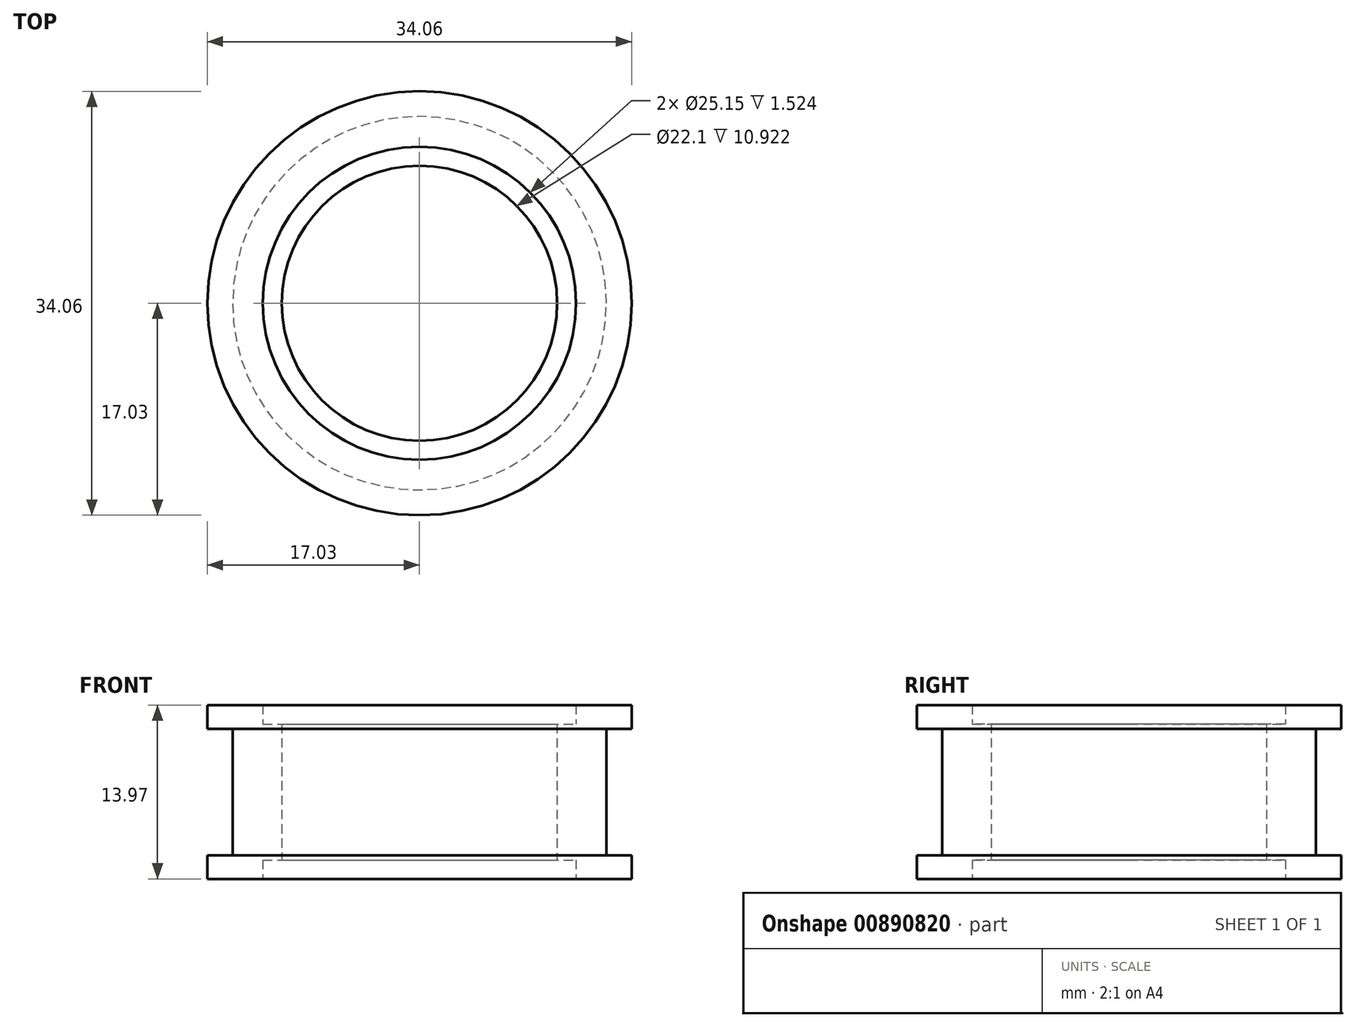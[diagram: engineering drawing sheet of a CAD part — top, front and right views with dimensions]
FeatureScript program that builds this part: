
annotation { "Feature Type Name" : "Feature", "Feature Type Description" : "" }
export const myFeature = defineFeature(function(context is Context, id is Id, definition is map)
    precondition{}
    {
        {
            var Q0;
            Q0=qCreatedBy(makeId("Front.planeOp"),FACE);
            var sketch = newSketch(context, id + "F0", { "sketchPlane" : qUnion([Q0])});
            skLineSegment(sketch, "E0", {"start": v(11.05, 17.27) * mm, "end": v(11.05, 6.35) * mm});
            skLineSegment(sketch, "E1", {"start": v(11.05, 17.27) * mm, "end": v(12.57, 17.27) * mm});
            skLineSegment(sketch, "E2", {"start": v(12.57, 17.27) * mm, "end": v(12.57, 18.8) * mm});
            skLineSegment(sketch, "E3", {"start": v(17.03, 16.89) * mm, "end": v(15, 16.89) * mm});
            skLineSegment(sketch, "E4", {"start": v(15, 16.89) * mm, "end": v(15, 6.73) * mm});
            skLineSegment(sketch, "E5", {"start": v(11.05, 6.35) * mm, "end": v(12.57, 6.35) * mm});
            skLineSegment(sketch, "E6", {"start": v(12.57, 6.35) * mm, "end": v(12.57, 4.82) * mm});
            skLineSegment(sketch, "E7", {"start": v(15, 6.73) * mm, "end": v(17.03, 6.73) * mm});
            skLineSegment(sketch, "E8", {"start": v(17.03, 6.73) * mm, "end": v(17.03, 4.82) * mm});
            skLineSegment(sketch, "E9", {"start": v(17.03, 4.82) * mm, "end": v(12.57, 4.82) * mm});
            skLineSegment(sketch, "E10", {"start": v(0, 0) * mm, "end": v(0, 28.1) * mm});
            skLineSegment(sketch, "E11", {"start": v(12.57, 18.8) * mm, "end": v(17.03, 18.8) * mm});
            skLineSegment(sketch, "E12", {"start": v(17.03, 18.8) * mm, "end": v(17.03, 16.89) * mm});
            skSolve(sketch);
        }
        {
            var Q0;
            Q0=makeQuery(id+"F0.imprint","IMPRINT",FACE,{"disambiguationData":[TD([[makeQuery(id+"F0.imprint","IMPRINT",EDGE,{"derivedFrom":sQuery(id+"F0.wireOp",EDGE,"E0")}),1.0]])]});
            var Q1;
            Q1=sQuery(id+"F0.wireOp",EDGE,"E10");
            revolve(context, id + "F1", {"surfaceOperationType" : NewSurfaceOperationType.NEW, "entities" : qUnion([Q0]), "axis" : qUnion([Q1]), "revolveType" : RevolveType.FULL});
        }
    });
